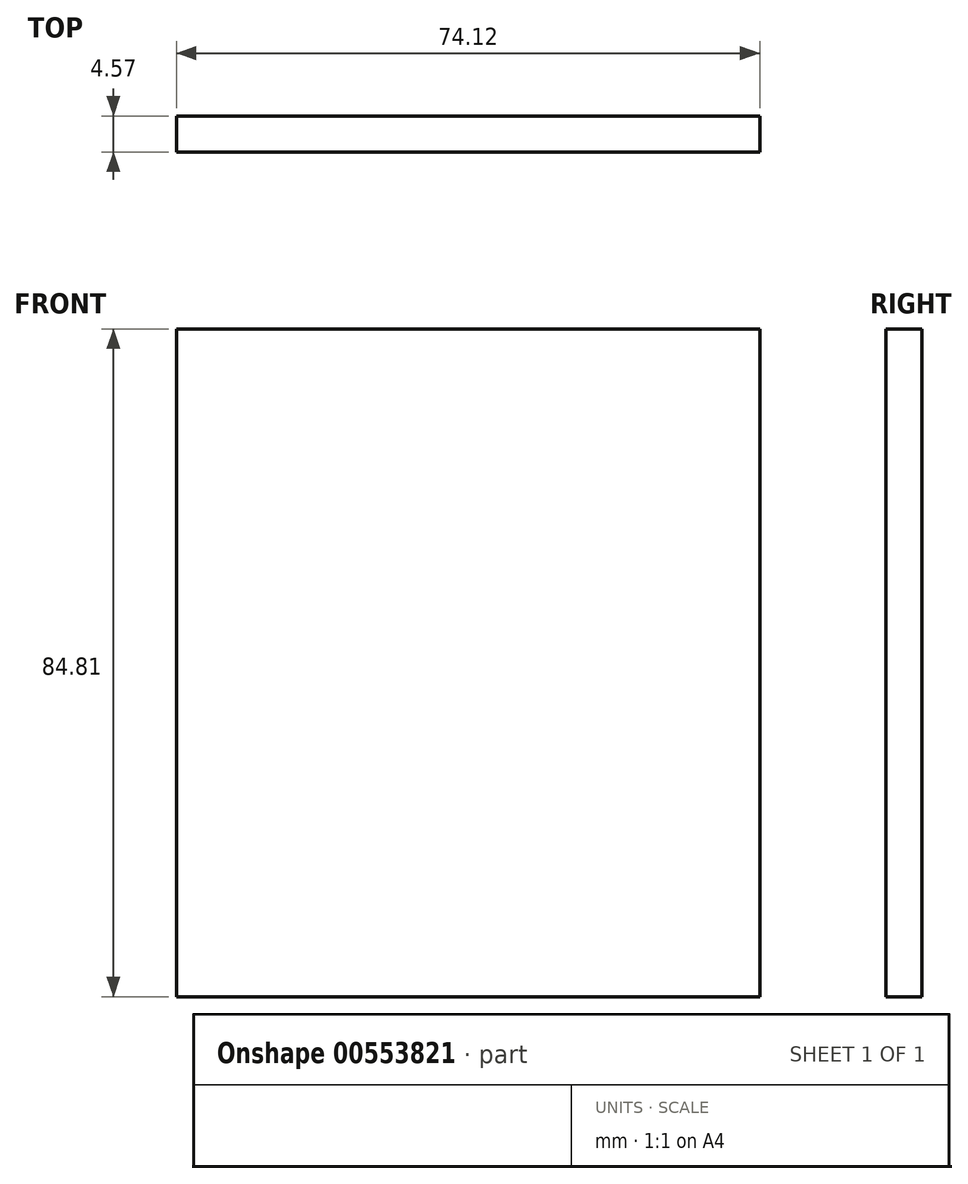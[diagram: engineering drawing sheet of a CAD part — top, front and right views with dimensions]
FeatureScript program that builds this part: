
annotation { "Feature Type Name" : "Feature", "Feature Type Description" : "" }
export const myFeature = defineFeature(function(context is Context, id is Id, definition is map)
    precondition{}
    {
        {
            var Q0;
            Q0=qCreatedBy(makeId("Front.planeOp"),FACE);
            var sketch = newSketch(context, id + "F0", { "sketchPlane" : qUnion([Q0])});
            skLineSegment(sketch, "E0.bottom", {"start": v(-74.12, 6.53) * mm, "end": v(0, 6.53) * mm});
            skLineSegment(sketch, "E0.top", {"start": v(-74.12, 91.34) * mm, "end": v(0, 91.34) * mm});
            skLineSegment(sketch, "E0.left", {"start": v(-74.12, 6.53) * mm, "end": v(-74.12, 91.34) * mm});
            skLineSegment(sketch, "E0.right", {"start": v(0, 6.53) * mm, "end": v(0, 91.34) * mm});
            skSolve(sketch);
        }
        {
            var Q0;
            Q0=makeQuery(id+"F0.imprint","IMPRINT",FACE,{"disambiguationData":[TD([[makeQuery(id+"F0.imprint","IMPRINT",EDGE,{"derivedFrom":sQuery(id+"F0.wireOp",EDGE,"E0.bottom")}),1.0]])]});
            extrude(context, id + "F1", {"entities" : qUnion([Q0]), "depth" : 0 * yard, "offsetDistance" : 0.03 * yard});
        }
    });
